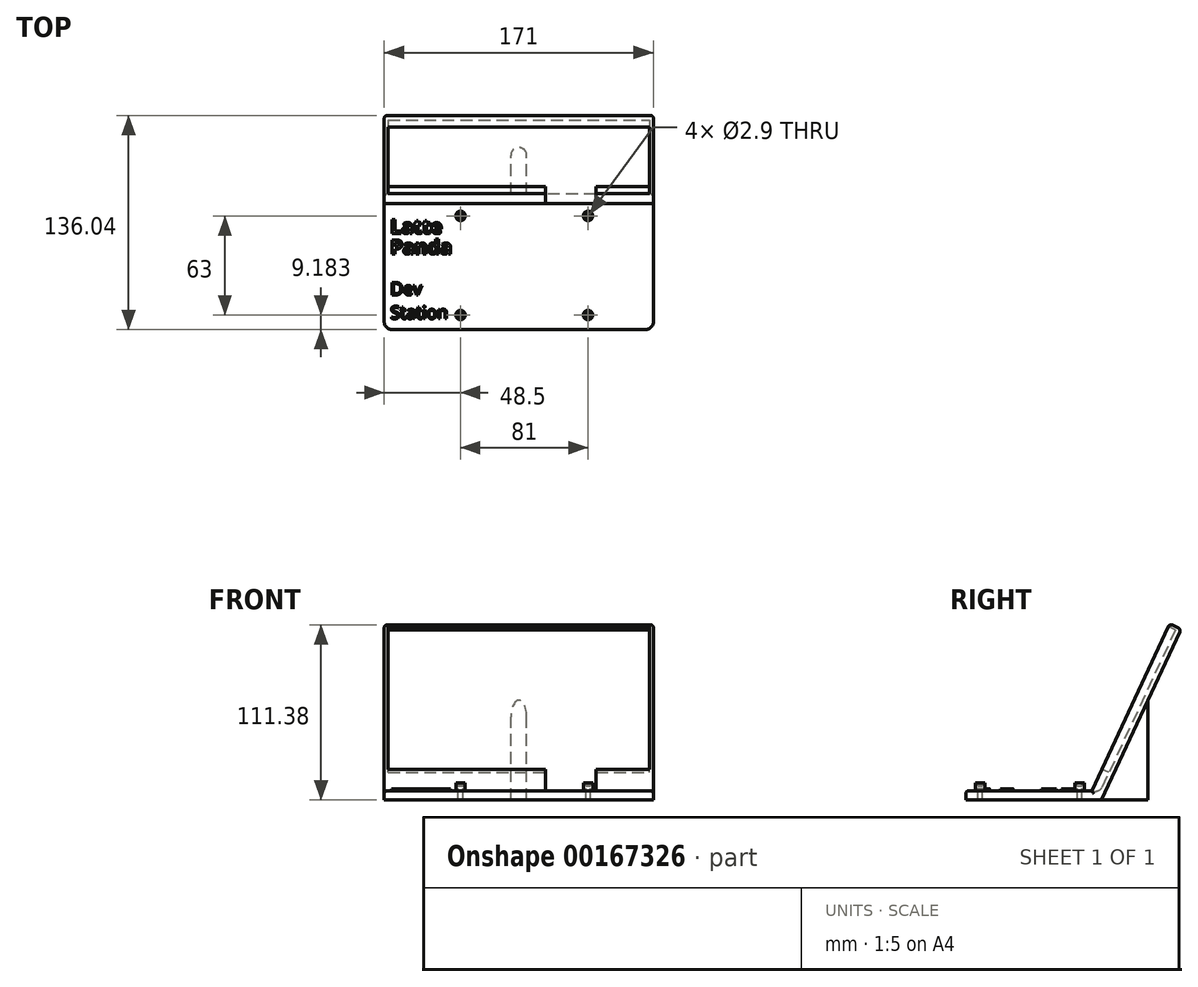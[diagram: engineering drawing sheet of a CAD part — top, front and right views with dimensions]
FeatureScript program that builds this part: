
annotation { "Feature Type Name" : "Feature", "Feature Type Description" : "" }
export const myFeature = defineFeature(function(context is Context, id is Id, definition is map)
    precondition{}
    {
        {
            var Q0;
            Q0=qCreatedBy(makeId("Right.planeOp"),FACE);
            var sketch = newSketch(context, id + "F0", { "sketchPlane" : qUnion([Q0])});
            skLineSegment(sketch, "E0", {"start": v(-47.86, -27.12) * mm, "end": v(38.17, -27.12) * mm});
            skLineSegment(sketch, "E1", {"start": v(38.17, -27.12) * mm, "end": v(88.84, 81.54) * mm});
            skLineSegment(sketch, "E2", {"start": v(88.84, 81.54) * mm, "end": v(81.6, 84.92) * mm});
            skLineSegment(sketch, "E3", {"start": v(81.6, 84.92) * mm, "end": v(32.14, -21.12) * mm});
            skLineSegment(sketch, "E4", {"start": v(32.14, -21.12) * mm, "end": v(-47.86, -21.12) * mm});
            skLineSegment(sketch, "E5", {"start": v(-47.86, -21.12) * mm, "end": v(-47.86, -27.12) * mm});
            skLineSegment(sketch, "E6", {"start": v(38.17, -27.12) * mm, "end": v(67.78, -27.12) * mm});
            skLineSegment(sketch, "E7", {"start": v(67.78, -27.12) * mm, "end": v(67.78, 36.38) * mm});
            skSolve(sketch);
        }
        {
            var Q0;
            Q0=makeQuery(id+"F0.imprint","IMPRINT",FACE,{"disambiguationData":[TD([[makeQuery(id+"F0.imprint","IMPRINT",EDGE,{"derivedFrom":sQuery(id+"F0.wireOp",EDGE,"E0")}),1.0]])]});
            extrude(context, id + "F1", {"entities" : qUnion([Q0]), "depth" : 85.5 * mm, "hasSecondDirection" : true, "secondDirectionOppositeDirection" : true, "secondDirectionDepth" : 85.5 * mm});
        }
        {
            var Q0;
            Q0=makeQuery(id+"F1.opExtrude","SWEPT_FACE",FACE,{"disambiguationData":[OSD([sQuery(id+"F0.wireOp",EDGE,"E3")])]});
            var sketch = newSketch(context, id + "F2", { "sketchPlane" : qUnion([Q0])});
            skLineSegment(sketch, "E8.bottom", {"start": v(-83, 109.44) * mm, "end": v(83, 109.44) * mm});
            skLineSegment(sketch, "E8.top", {"start": v(-83, 9.44) * mm, "end": v(83, 9.44) * mm});
            skLineSegment(sketch, "E8.left", {"start": v(-83, 109.44) * mm, "end": v(-83, 9.44) * mm});
            skLineSegment(sketch, "E8.right", {"start": v(83, 109.44) * mm, "end": v(83, 9.44) * mm});
            skLineSegment(sketch, "E9", {"start": v(49, 9.44) * mm, "end": v(49, -5.56) * mm});
            skLineSegment(sketch, "E10", {"start": v(49, -5.56) * mm, "end": v(17, -5.56) * mm});
            skLineSegment(sketch, "E11", {"start": v(17, -5.56) * mm, "end": v(17, 9.44) * mm});
            skSolve(sketch);
        }
        {
            var Q0;
            Q0=makeQuery(id+"F2.imprint","IMPRINT",FACE,{"disambiguationData":[TD([[makeQuery(id+"F2.imprint","IMPRINT",EDGE,{"derivedFrom":sQuery(id+"F2.wireOp",EDGE,"E8.bottom")}),-1.0]])]});
            var Q1;
            {var subQ0=sQuery(id+"F2.wireOp",EDGE,"E9");Q1=makeQuery(id+"F2.imprint","IMPRINT",FACE,{"disambiguationData":[TD([[makeQuery(id+"F2.imprint","IMPRINT",EDGE,{"derivedFrom":subQ0}),-1.0]])]});}
            extrude(context, id + "F3", {"entities" : qUnion([Q0, Q1]), "operationType" : NewBodyOperationType.REMOVE, "oppositeDirection" : true, "depth" : 5 * mm});
        }
        {
            var Q0;
            Q0=makeQuery(id+"F1.opExtrude","CAP_EDGE",EDGE,{"disambiguationData":[OSD([sQuery(id+"F0.wireOp",EDGE,"E2")])],"isStart":true});
            var Q1;
            Q1=makeQuery(id+"F1.opExtrude","CAP_EDGE",EDGE,{"disambiguationData":[OSD([sQuery(id+"F0.wireOp",EDGE,"E2")])],"isStart":false});
            var Q2;
            Q2=makeQuery(id+"F1.opExtrude","CAP_EDGE",EDGE,{"disambiguationData":[OSD([sQuery(id+"F0.wireOp",EDGE,"E1")])],"isStart":false});
            var Q3;
            Q3=makeQuery(id+"F1.opExtrude","SWEPT_EDGE",EDGE,{"disambiguationData":[OSD([sQuery(id+"F0.wireOp",EDGE,"E1"),sQuery(id+"F0.wireOp",EDGE,"E2")])]});
            var Q4;
            Q4=makeQuery(id+"F1.opExtrude","CAP_EDGE",EDGE,{"disambiguationData":[OSD([sQuery(id+"F0.wireOp",EDGE,"E1")])],"isStart":true});
            var Q5;
            Q5=makeQuery(id+"F1.opExtrude","CAP_EDGE",EDGE,{"disambiguationData":[OSD([sQuery(id+"F0.wireOp",EDGE,"E3")])],"isStart":false});
            var Q6;
            Q6=makeQuery(id+"F1.opExtrude","CAP_EDGE",EDGE,{"disambiguationData":[OSD([sQuery(id+"F0.wireOp",EDGE,"E4")])],"isStart":false});
            var Q7;
            Q7=makeQuery(id+"F1.opExtrude","SWEPT_EDGE",EDGE,{"disambiguationData":[OSD([sQuery(id+"F0.wireOp",EDGE,"E4"),sQuery(id+"F0.wireOp",EDGE,"E5")])]});
            var Q8;
            Q8=makeQuery(id+"F1.opExtrude","CAP_EDGE",EDGE,{"disambiguationData":[OSD([sQuery(id+"F0.wireOp",EDGE,"E4")])],"isStart":true});
            var Q9;
            Q9=makeQuery(id+"F1.opExtrude","SWEPT_EDGE",EDGE,{"disambiguationData":[OSD([sQuery(id+"F0.wireOp",EDGE,"E2"),sQuery(id+"F0.wireOp",EDGE,"E3")])]});
            var Q10;
            Q10=makeQuery(id+"F1.opExtrude","CAP_EDGE",EDGE,{"disambiguationData":[OSD([sQuery(id+"F0.wireOp",EDGE,"E3")])],"isStart":true});
            fillet(context, id + "F4", {"entities" : qUnion([Q0, Q1, Q2, Q3, Q4, Q5, Q6, Q7, Q8, Q9, Q10]), "radius" : 2 * mm, "tangentPropagation" : true, "allowEdgeOverflow" : false});
        }
        {
            var Q0;
            Q0=makeQuery(id+"F1.opExtrude","SWEPT_FACE",FACE,{"disambiguationData":[OSD([sQuery(id+"F0.wireOp",EDGE,"E4")])]});
            var sketch = newSketch(context, id + "F5", { "sketchPlane" : qUnion([Q0])});
            skLineSegment(sketch, "E12.bottom", {"start": v(-40.5, 27.82) * mm, "end": v(47.5, 27.82) * mm});
            skLineSegment(sketch, "E12.top", {"start": v(-40.5, -42.18) * mm, "end": v(47.5, -42.18) * mm});
            skLineSegment(sketch, "E12.left", {"start": v(-40.5, 27.82) * mm, "end": v(-40.5, -42.18) * mm});
            skLineSegment(sketch, "E12.right", {"start": v(47.5, 27.82) * mm, "end": v(47.5, -42.18) * mm});
            skLineSegment(sketch, "E13.bottom", {"start": v(-37, 24.32) * mm, "end": v(44, 24.32) * mm});
            skLineSegment(sketch, "E13.top", {"start": v(-37, -38.68) * mm, "end": v(44, -38.68) * mm});
            skLineSegment(sketch, "E13.left", {"start": v(-37, 24.32) * mm, "end": v(-37, -38.68) * mm});
            skLineSegment(sketch, "E13.right", {"start": v(44, 24.32) * mm, "end": v(44, -38.68) * mm});
            skCircle(sketch, "E14", {"center": v(44, 24.32) * mm, "radius": 3 * mm});
            skCircle(sketch, "E15", {"center": v(44, 24.32) * mm, "radius": 1.45 * mm});
            skCircle(sketch, "E16", {"center": v(44, -38.68) * mm, "radius": 3 * mm});
            skCircle(sketch, "E17", {"center": v(44, -38.68) * mm, "radius": 1.45 * mm});
            skCircle(sketch, "E18", {"center": v(-37, -38.68) * mm, "radius": 3 * mm});
            skCircle(sketch, "E19", {"center": v(-37, -38.68) * mm, "radius": 1.45 * mm});
            skCircle(sketch, "E20", {"center": v(-37, 24.32) * mm, "radius": 3 * mm});
            skCircle(sketch, "E21", {"center": v(-37, 24.32) * mm, "radius": 1.45 * mm});
            skSolve(sketch);
        }
        {
            var Q0;
            {var subQ0=sQuery(id+"F5.wireOp",EDGE,"E13.right");var subQ1=sQuery(id+"F5.wireOp",EDGE,"E13.bottom");var subQ2=makeQuery(id+"F5.imprint","INTERSECT",VERTEX,{"derivedFrom":[subQ1,subQ0]});Q0=makeQuery(id+"F5.imprint","IMPRINT",FACE,{"disambiguationData":[TD([[makeQuery(id+"F5.imprint","IMPRINT",EDGE,{"disambiguationData":[TD([[subQ2,1.0]])],"derivedFrom":subQ1}),1.0]])]});}
            var Q1;
            {var subQ0=sQuery(id+"F5.wireOp",EDGE,"E13.right");var subQ1=sQuery(id+"F5.wireOp",EDGE,"E13.bottom");var subQ2=makeQuery(id+"F5.imprint","INTERSECT",VERTEX,{"derivedFrom":[subQ1,subQ0]});Q1=makeQuery(id+"F5.imprint","IMPRINT",FACE,{"disambiguationData":[TD([[makeQuery(id+"F5.imprint","IMPRINT",EDGE,{"disambiguationData":[TD([[subQ2,1.0]])],"derivedFrom":subQ1}),-1.0]])]});}
            var Q2;
            {var subQ0=sQuery(id+"F5.wireOp",EDGE,"E13.left");var subQ1=sQuery(id+"F5.wireOp",EDGE,"E13.bottom");var subQ2=makeQuery(id+"F5.imprint","INTERSECT",VERTEX,{"derivedFrom":[subQ1,subQ0]});Q2=makeQuery(id+"F5.imprint","IMPRINT",FACE,{"disambiguationData":[TD([[makeQuery(id+"F5.imprint","IMPRINT",EDGE,{"disambiguationData":[TD([[subQ2,-1.0]])],"derivedFrom":subQ1}),1.0]])]});}
            var Q3;
            {var subQ0=sQuery(id+"F5.wireOp",EDGE,"E13.left");var subQ1=sQuery(id+"F5.wireOp",EDGE,"E13.bottom");var subQ2=makeQuery(id+"F5.imprint","INTERSECT",VERTEX,{"derivedFrom":[subQ1,subQ0]});Q3=makeQuery(id+"F5.imprint","IMPRINT",FACE,{"disambiguationData":[TD([[makeQuery(id+"F5.imprint","IMPRINT",EDGE,{"disambiguationData":[TD([[subQ2,-1.0]])],"derivedFrom":subQ1}),-1.0]])]});}
            var Q4;
            {var subQ0=sQuery(id+"F5.wireOp",EDGE,"E13.left");var subQ1=sQuery(id+"F5.wireOp",EDGE,"E13.top");var subQ2=makeQuery(id+"F5.imprint","INTERSECT",VERTEX,{"derivedFrom":[subQ1,subQ0]});Q4=makeQuery(id+"F5.imprint","IMPRINT",FACE,{"disambiguationData":[TD([[makeQuery(id+"F5.imprint","IMPRINT",EDGE,{"disambiguationData":[TD([[subQ2,-1.0]])],"derivedFrom":subQ1}),-1.0]])]});}
            var Q5;
            {var subQ0=sQuery(id+"F5.wireOp",EDGE,"E13.left");var subQ1=sQuery(id+"F5.wireOp",EDGE,"E13.top");var subQ2=makeQuery(id+"F5.imprint","INTERSECT",VERTEX,{"derivedFrom":[subQ1,subQ0]});Q5=makeQuery(id+"F5.imprint","IMPRINT",FACE,{"disambiguationData":[TD([[makeQuery(id+"F5.imprint","IMPRINT",EDGE,{"disambiguationData":[TD([[subQ2,-1.0]])],"derivedFrom":subQ1}),1.0]])]});}
            var Q6;
            {var subQ0=sQuery(id+"F5.wireOp",EDGE,"E13.right");var subQ1=sQuery(id+"F5.wireOp",EDGE,"E13.top");var subQ2=makeQuery(id+"F5.imprint","INTERSECT",VERTEX,{"derivedFrom":[subQ1,subQ0]});Q6=makeQuery(id+"F5.imprint","IMPRINT",FACE,{"disambiguationData":[TD([[makeQuery(id+"F5.imprint","IMPRINT",EDGE,{"disambiguationData":[TD([[subQ2,1.0]])],"derivedFrom":subQ1}),-1.0]])]});}
            var Q7;
            {var subQ0=sQuery(id+"F5.wireOp",EDGE,"E13.right");var subQ1=sQuery(id+"F5.wireOp",EDGE,"E13.top");var subQ2=makeQuery(id+"F5.imprint","INTERSECT",VERTEX,{"derivedFrom":[subQ1,subQ0]});Q7=makeQuery(id+"F5.imprint","IMPRINT",FACE,{"disambiguationData":[TD([[makeQuery(id+"F5.imprint","IMPRINT",EDGE,{"disambiguationData":[TD([[subQ2,1.0]])],"derivedFrom":subQ1}),1.0]])]});}
            extrude(context, id + "F6", {"entities" : qUnion([Q0, Q1, Q2, Q3, Q4, Q5, Q6, Q7]), "operationType" : NewBodyOperationType.REMOVE, "endBound" : BoundingType.THROUGH_ALL, "oppositeDirection" : true, "depth" : 5 * mm});
        }
        {
            var Q0;
            {var subQ0=sQuery(id+"F5.wireOp",EDGE,"E21");var subQ1=sQuery(id+"F5.wireOp",EDGE,"E13.bottom");var subQ2=makeQuery(id+"F5.imprint","INTERSECT",VERTEX,{"derivedFrom":[subQ1,subQ0]});Q0=makeQuery(id+"F5.imprint","IMPRINT",FACE,{"disambiguationData":[TD([[makeQuery(id+"F5.imprint","IMPRINT",EDGE,{"disambiguationData":[TD([[subQ2,-1.0]])],"derivedFrom":subQ1}),1.0]])]});}
            var Q1;
            {var subQ0=sQuery(id+"F5.wireOp",EDGE,"E21");var subQ1=sQuery(id+"F5.wireOp",EDGE,"E13.bottom");var subQ2=makeQuery(id+"F5.imprint","INTERSECT",VERTEX,{"derivedFrom":[subQ1,subQ0]});Q1=makeQuery(id+"F5.imprint","IMPRINT",FACE,{"disambiguationData":[TD([[makeQuery(id+"F5.imprint","IMPRINT",EDGE,{"disambiguationData":[TD([[subQ2,-1.0]])],"derivedFrom":subQ1}),-1.0]])]});}
            var Q2;
            {var subQ0=sQuery(id+"F5.wireOp",EDGE,"E14");var subQ1=sQuery(id+"F5.wireOp",EDGE,"E13.bottom");var subQ2=makeQuery(id+"F5.imprint","INTERSECT",VERTEX,{"derivedFrom":[subQ1,subQ0]});Q2=makeQuery(id+"F5.imprint","IMPRINT",FACE,{"disambiguationData":[TD([[makeQuery(id+"F5.imprint","IMPRINT",EDGE,{"disambiguationData":[TD([[subQ2,-1.0]])],"derivedFrom":subQ1}),1.0]])]});}
            var Q3;
            {var subQ0=sQuery(id+"F5.wireOp",EDGE,"E14");var subQ1=sQuery(id+"F5.wireOp",EDGE,"E13.bottom");var subQ2=makeQuery(id+"F5.imprint","INTERSECT",VERTEX,{"derivedFrom":[subQ1,subQ0]});Q3=makeQuery(id+"F5.imprint","IMPRINT",FACE,{"disambiguationData":[TD([[makeQuery(id+"F5.imprint","IMPRINT",EDGE,{"disambiguationData":[TD([[subQ2,-1.0]])],"derivedFrom":subQ1}),-1.0]])]});}
            var Q4;
            {var subQ0=sQuery(id+"F5.wireOp",EDGE,"E19");var subQ1=sQuery(id+"F5.wireOp",EDGE,"E13.top");var subQ2=makeQuery(id+"F5.imprint","INTERSECT",VERTEX,{"derivedFrom":[subQ1,subQ0]});Q4=makeQuery(id+"F5.imprint","IMPRINT",FACE,{"disambiguationData":[TD([[makeQuery(id+"F5.imprint","IMPRINT",EDGE,{"disambiguationData":[TD([[subQ2,-1.0]])],"derivedFrom":subQ1}),1.0]])]});}
            var Q5;
            {var subQ0=sQuery(id+"F5.wireOp",EDGE,"E19");var subQ1=sQuery(id+"F5.wireOp",EDGE,"E13.top");var subQ2=makeQuery(id+"F5.imprint","INTERSECT",VERTEX,{"derivedFrom":[subQ1,subQ0]});Q5=makeQuery(id+"F5.imprint","IMPRINT",FACE,{"disambiguationData":[TD([[makeQuery(id+"F5.imprint","IMPRINT",EDGE,{"disambiguationData":[TD([[subQ2,-1.0]])],"derivedFrom":subQ1}),-1.0]])]});}
            var Q6;
            {var subQ0=sQuery(id+"F5.wireOp",EDGE,"E16");var subQ1=sQuery(id+"F5.wireOp",EDGE,"E13.top");var subQ2=makeQuery(id+"F5.imprint","INTERSECT",VERTEX,{"derivedFrom":[subQ1,subQ0]});Q6=makeQuery(id+"F5.imprint","IMPRINT",FACE,{"disambiguationData":[TD([[makeQuery(id+"F5.imprint","IMPRINT",EDGE,{"disambiguationData":[TD([[subQ2,-1.0]])],"derivedFrom":subQ1}),1.0]])]});}
            var Q7;
            {var subQ0=sQuery(id+"F5.wireOp",EDGE,"E16");var subQ1=sQuery(id+"F5.wireOp",EDGE,"E13.top");var subQ2=makeQuery(id+"F5.imprint","INTERSECT",VERTEX,{"derivedFrom":[subQ1,subQ0]});Q7=makeQuery(id+"F5.imprint","IMPRINT",FACE,{"disambiguationData":[TD([[makeQuery(id+"F5.imprint","IMPRINT",EDGE,{"disambiguationData":[TD([[subQ2,-1.0]])],"derivedFrom":subQ1}),-1.0]])]});}
            extrude(context, id + "F7", {"entities" : qUnion([Q0, Q1, Q2, Q3, Q4, Q5, Q6, Q7]), "operationType" : NewBodyOperationType.ADD, "depth" : 5 * mm});
        }
        {
            var Q0;
            {var subQ0=sQuery(id+"F0.wireOp",EDGE,"E6");Q0=makeQuery(id+"F0.imprint","IMPRINT",FACE,{"disambiguationData":[TD([[makeQuery(id+"F0.imprint","IMPRINT",EDGE,{"derivedFrom":subQ0}),1.0]])]});}
            extrude(context, id + "F8", {"entities" : qUnion([Q0]), "operationType" : NewBodyOperationType.ADD, "depth" : 5 * mm, "hasSecondDirection" : true, "secondDirectionOppositeDirection" : true, "secondDirectionDepth" : 5 * mm});
        }
        {
            var Q0;
            Q0=makeQuery(id+"F8.opExtrude","CAP_EDGE",EDGE,{"disambiguationData":[OSD([sQuery(id+"F0.wireOp",EDGE,"E7")])],"isStart":false});
            var Q1;
            Q1=makeQuery(id+"F8.opExtrude","CAP_EDGE",EDGE,{"disambiguationData":[OSD([sQuery(id+"F0.wireOp",EDGE,"E7")])],"isStart":true});
            fillet(context, id + "F9", {"entities" : qUnion([Q0, Q1]), "radius" : 5 * mm, "tangentPropagation" : true, "allowEdgeOverflow" : false});
        }
        {
            var Q0;
            Q0=makeQuery(id+"F3.boolean.opBoolean","COPY",EDGE,{"derivedFrom":makeQuery(id+"F3.opExtrude","CAP_EDGE",EDGE,{"disambiguationData":[OSD([sQuery(id+"F2.wireOp",EDGE,"E10")])],"isStart":false})});
            fillet(context, id + "F10", {"entities" : qUnion([Q0]), "radius" : 5 * mm, "tangentPropagation" : true, "allowEdgeOverflow" : false});
        }
        {
            var Q0;
            Q0=makeQuery(id+"F1.opExtrude","CAP_EDGE",EDGE,{"disambiguationData":[OSD([sQuery(id+"F0.wireOp",EDGE,"E5")])],"isStart":false});
            var Q1;
            Q1=makeQuery(id+"F1.opExtrude","CAP_EDGE",EDGE,{"disambiguationData":[OSD([sQuery(id+"F0.wireOp",EDGE,"E5")])],"isStart":true});
            fillet(context, id + "F11", {"entities" : qUnion([Q0, Q1]), "radius" : 5 * mm, "tangentPropagation" : true, "allowEdgeOverflow" : false});
        }
        {
            var Q0;
            Q0=makeQuery(id+"F7.opExtrude","CAP_EDGE",EDGE,{"disambiguationData":[OSD([sQuery(id+"F5.wireOp",EDGE,"E19")])],"isStart":false});
            var Q1;
            Q1=makeQuery(id+"F7.opExtrude","CAP_EDGE",EDGE,{"disambiguationData":[OSD([sQuery(id+"F5.wireOp",EDGE,"E21")])],"isStart":false});
            var Q2;
            Q2=makeQuery(id+"F7.opExtrude","CAP_EDGE",EDGE,{"disambiguationData":[OSD([sQuery(id+"F5.wireOp",EDGE,"E17")])],"isStart":false});
            var Q3;
            Q3=makeQuery(id+"F7.opExtrude","CAP_EDGE",EDGE,{"disambiguationData":[OSD([sQuery(id+"F5.wireOp",EDGE,"E15")])],"isStart":false});
            chamfer(context, id + "F12", {"entities" : qUnion([Q0, Q1, Q2, Q3]), "chamferType" : ChamferType.TWO_OFFSETS, "width1" : 2 * mm, "oppositeDirection" : false, "width2" : .2 * mm, "tangentPropagation" : true});
        }
        {
            var Q0;
            Q0=makeQuery(id+"F5.imprint","IMPRINT",FACE,{"disambiguationData":[TD([[makeQuery(id+"F5.imprint","IMPRINT",EDGE,{"derivedFrom":sQuery(id+"F5.wireOp",EDGE,"E12.bottom")}),1.0]])]});
            var sketch = newSketch(context, id + "F13", { "sketchPlane" : qUnion([Q0])});
            skText(sketch, "E22", { "text": "Latte", "fontName": "OpenSans-Bold.ttf"});
            skText(sketch, "E23", { "text": "Panda", "fontName": "OpenSans-Bold.ttf"});
            skPoint(sketch, "E23.firstSnap0", {"position": v(-81.5, 17.64) * mm});
            skText(sketch, "E24", { "text": "Dev\nStation", "fontName": "OpenSans-Regular.ttf"});
            const initialGuessF13  = {"E22": [-0.0815, 0.01314, 1, 0, 0.009], "E23": [-0.0815, 0.00014, 1, 0, 0.009], "E24": [-0.0815, -0.02586, 1, 0, 0.008]};
            skSetInitialGuess(sketch, initialGuessF13);
            skSolve(sketch);
        }
        {
            var Q0;
            Q0 = qSketchRegion(id + "F13", true);
            extrude(context, id + "F14", {"entities" : qUnion([Q0]), "operationType" : NewBodyOperationType.ADD, "depth" : 1.2 * mm});
        }
    });
